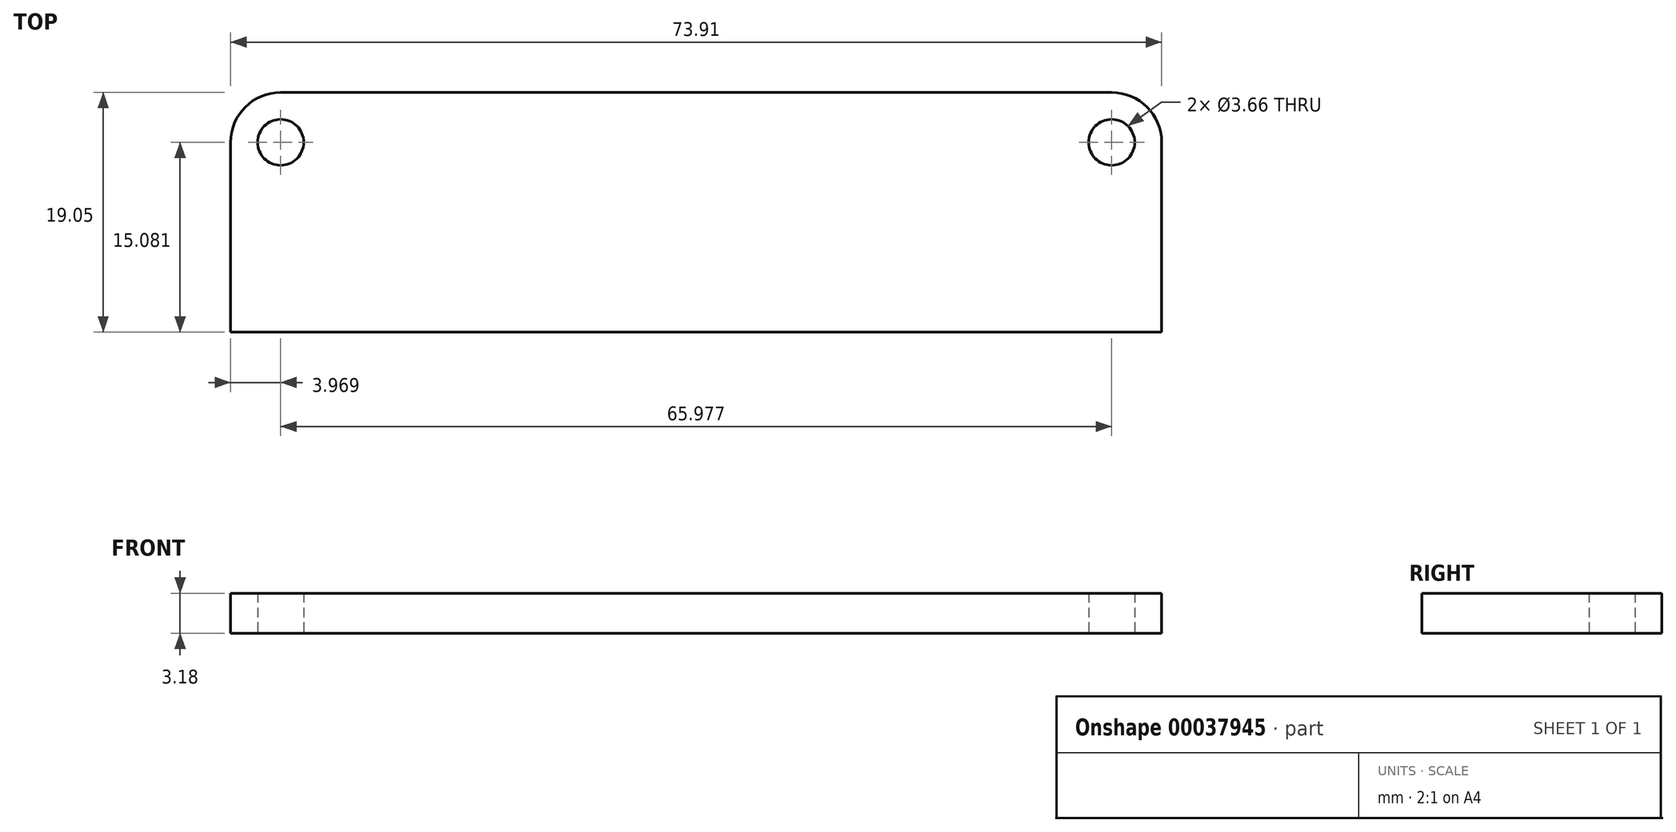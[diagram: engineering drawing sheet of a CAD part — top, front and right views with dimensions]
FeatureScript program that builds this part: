
annotation { "Feature Type Name" : "Feature", "Feature Type Description" : "" }
export const myFeature = defineFeature(function(context is Context, id is Id, definition is map)
    precondition{}
    {
        {
            var Q0;
            Q0=qCreatedBy(makeId("Top.planeOp"),FACE);
            var sketch = newSketch(context, id + "F0", { "sketchPlane" : qUnion([Q0])});
            skLineSegment(sketch, "E0.bottom", {"start": v(0, 0) * mm, "end": v(73.91, 0) * mm});
            skLineSegment(sketch, "E0.top", {"start": v(0, -19.05) * mm, "end": v(73.91, -19.05) * mm});
            skLineSegment(sketch, "E0.left", {"start": v(0, 0) * mm, "end": v(0, -19.05) * mm});
            skLineSegment(sketch, "E0.right", {"start": v(73.91, 0) * mm, "end": v(73.91, -19.05) * mm});
            skLineSegment(sketch, "E1", {"start": v(3.97, 0) * mm, "end": v(3.97, -3.97) * mm, "construction": true});
            skLineSegment(sketch, "E2", {"start": v(3.97, -3.97) * mm, "end": v(0, -3.97) * mm, "construction": true});
            skLineSegment(sketch, "E3", {"start": v(73.91, -3.97) * mm, "end": v(69.95, -3.97) * mm, "construction": true});
            skLineSegment(sketch, "E4", {"start": v(3.97, -3.97) * mm, "end": v(69.95, -3.97) * mm, "construction": true});
            skCircle(sketch, "E5", {"center": v(3.97, -3.97) * mm, "radius": 1.83 * mm});
            skCircle(sketch, "E6", {"center": v(69.95, -3.97) * mm, "radius": 1.83 * mm});
            skSolve(sketch);
        }
        {
            var Q0;
            Q0 = qSketchRegion(id + "F0", true);
            extrude(context, id + "F1", {"entities" : qUnion([Q0]), "depth" : 3.17 * mm});
        }
        {
            var Q0;
            Q0=makeQuery(id+"F1.opExtrude","SWEPT_EDGE",EDGE,{"disambiguationData":[OSD([sQuery(id+"F0.wireOp",EDGE,"E0.bottom"),sQuery(id+"F0.wireOp",EDGE,"E0.left")])]});
            var Q1;
            Q1=makeQuery(id+"F1.opExtrude","SWEPT_EDGE",EDGE,{"disambiguationData":[OSD([sQuery(id+"F0.wireOp",EDGE,"E0.bottom"),sQuery(id+"F0.wireOp",EDGE,"E0.right")])]});
            fillet(context, id + "F2", {"entities" : qUnion([Q0, Q1]), "radius" : 3.97 * mm, "tangentPropagation" : true, "allowEdgeOverflow" : false});
        }
    });
